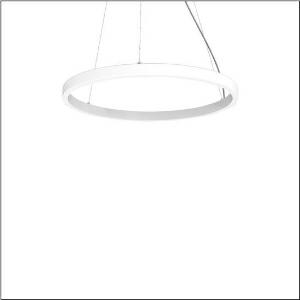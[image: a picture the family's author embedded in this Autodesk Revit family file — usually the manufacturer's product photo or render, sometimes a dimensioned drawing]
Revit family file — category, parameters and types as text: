
# Revit family: silica_r__21_ring-o_5pjbo3d3004a_bcd7
name_source: partatom
category: Lighting Fixtures
units: mm (PartAtom-declared; Revit-internal decimal feet)

## family parameters
Cut with Voids When Loaded = No
Host = Face
Light Source = No
Part Type = Normal
Room Calculation Point = No
Round Connector Dimension = Use Diameter
Shared = No

## types (1)
- Silica® 21 Ring-O (1 x LED, 7210 lm, 105 W, 4000K)
    Apparent Load = 105 VA
    CIE Flux Codes = 2 16 49 50 100
    Color Rendering = 80
    Color Temperature = 4000K
    Default Elevation = 1800 mm
    Description = Silica® 21 Ring-O, suspended luminaire, of PMMA, frosted, light emission: outer ring side luminous distribution, primary light characteristic: symmetric, installation type: suspended mounting, LED, rated luminous flux: 7.210lm, luminous efficacy: 69lm/W, light colour: 840, colour temperature: 4000K, control gear: DALI 2, with terminal, 5-pole, mains connection: 230V, AC/DC, 0/50..60Hz, rated input power: 105W, housing, of extruded aluminium section, traffic white (RAL 9016), diameter: 1.100mm, ceiling canopy, traffic white (RAL 9016), protection rating (lamp compartment): IP40, insulation class (complete): insulation class I (protective earthing), certification: CE, impact resistance: IK02, permissible operating ambient temperature: 0..+35°C, packaging unit: 1 piece
    Height = 48 mm  [stored 0.15748 ft]
    Lamp = 1 x LED
    Lamp Light Flux = 7210 lm
    Lamp Power = 105 W
    Lamp count = 1
    Length = 1100 mm
    Luminous efficacy = 69 lm/W
    Manufacturer = Siteco
    ModVariant = No
    Model = 5PJBO3D3004A
    Mounting Place = Ceiling
    Mounting Type = Pendant
    Number of Poles = 1
    OnlyDefault = Yes
    Power Factor = 1
    Product Name = Silica® 21 Ring-O
    Product group = suspended luminaire
    ProductGroupID = 905
    Protection Class = Protection class I
    Protection Degree = IP 40
    RLX_Detail_Level = 1
    RLX_Emergency_Light_Flux = 0 lm
    RLX_Emergency_Type = 0
    RLX_Emergency_Type_DB = No
    RlxData = <blob elided: 13537 chars, md5=0f420fd0>
    Socket = socket
    Standby Power = 0 W
    System Light Flux = 7210 lm
    System Power = 105 W
    Type Comments = Product without accessories
    Type Image = l_1258387.jpg
    URL = http://relux.com
    VarID = ---
    Voltage = 0 V
    Weight = 0.00 kg
    Width = 0 mm  [stored 0 ft]

note: [stored X ft] marks values corroborated as IEEE doubles in the binary element streams (Revit-internal decimal feet)

## geometry (parser evidence)
native form markers: Sweep x11
no freeform markers — native parametric forms only
